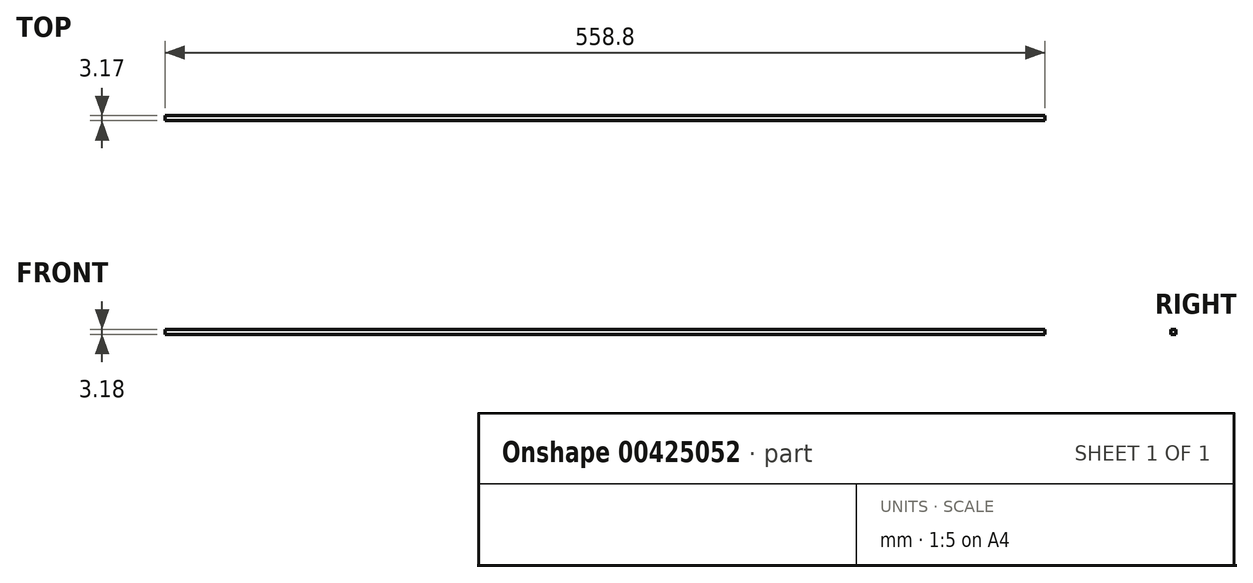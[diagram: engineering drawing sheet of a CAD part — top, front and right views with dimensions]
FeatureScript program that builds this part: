
annotation { "Feature Type Name" : "Feature", "Feature Type Description" : "" }
export const myFeature = defineFeature(function(context is Context, id is Id, definition is map)
    precondition{}
    {
        {
            var Q0;
            Q0=qCreatedBy(makeId("Front.planeOp"),FACE);
            var sketch = newSketch(context, id + "F0", { "sketchPlane" : qUnion([Q0])});
            skLineSegment(sketch, "E0.bottom", {"start": v(-316.46, -27.74) * mm, "end": v(242.34, -27.74) * mm});
            skLineSegment(sketch, "E0.top", {"start": v(-316.46, -30.92) * mm, "end": v(242.34, -30.92) * mm});
            skLineSegment(sketch, "E0.left", {"start": v(-316.46, -27.74) * mm, "end": v(-316.46, -30.92) * mm});
            skLineSegment(sketch, "E0.right", {"start": v(242.34, -27.74) * mm, "end": v(242.34, -30.92) * mm});
            skSolve(sketch);
        }
        {
            var Q0;
            Q0 = qSketchRegion(id + "F0", true);
            extrude(context, id + "F1", {"entities" : qUnion([Q0]), "depth" : 3.17 * mm});
        }
    });
